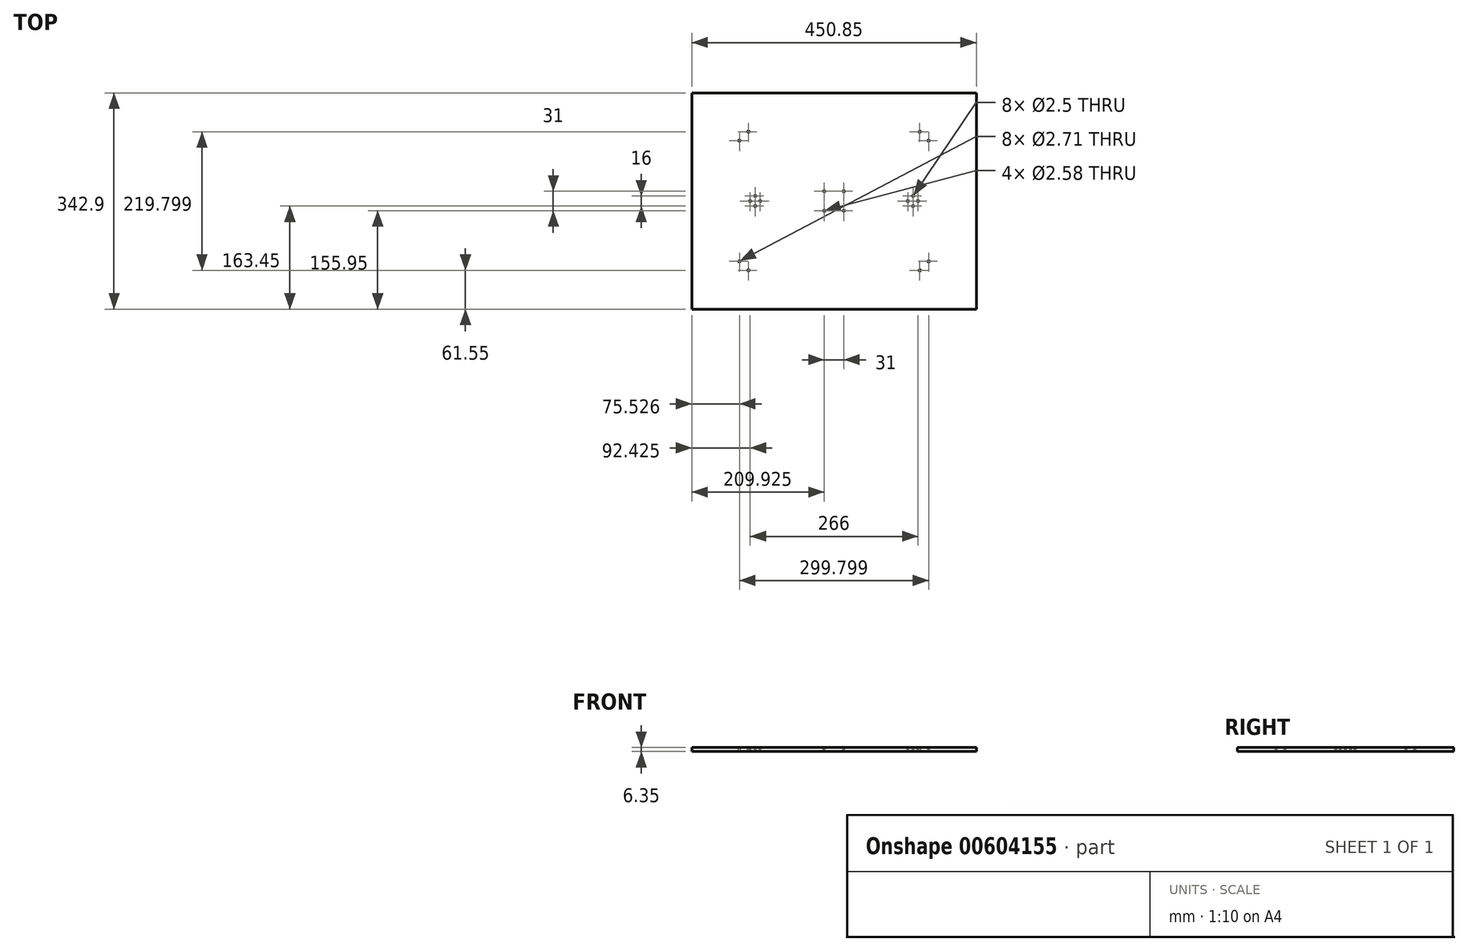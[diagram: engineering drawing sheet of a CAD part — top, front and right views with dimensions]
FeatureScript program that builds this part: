
annotation { "Feature Type Name" : "Feature", "Feature Type Description" : "" }
export const myFeature = defineFeature(function(context is Context, id is Id, definition is map)
    precondition{}
    {
        {
            var Q0;
            Q0=qCreatedBy(makeId("Top.planeOp"),FACE);
            var sketch = newSketch(context, id + "F0", { "sketchPlane" : qUnion([Q0])});
            skLineSegment(sketch, "E0.bottom", {"start": v(0, 0) * mm, "end": v(-450.85, 0) * mm});
            skLineSegment(sketch, "E0.top", {"start": v(0, -342.9) * mm, "end": v(-450.85, -342.9) * mm});
            skLineSegment(sketch, "E0.left", {"start": v(0, 0) * mm, "end": v(0, -342.9) * mm});
            skLineSegment(sketch, "E0.right", {"start": v(-450.85, 0) * mm, "end": v(-450.85, -342.9) * mm});
            skSolve(sketch);
        }
        {
            var Q0;
            Q0 = qSketchRegion(id + "F0", true);
            extrude(context, id + "F1", {"entities" : qUnion([Q0]), "depth" : 6.35 * mm, "offsetDistance" : 25 * mm});
        }
        {
            var Q0;
            Q0=makeQuery(id+"F1.opExtrude","CAP_FACE",FACE,{"disambiguationData":[OSD([sQuery(id+"F0.wireOp",EDGE,"E0.bottom"),sQuery(id+"F0.wireOp",EDGE,"E0.top"),sQuery(id+"F0.wireOp",EDGE,"E0.left"),sQuery(id+"F0.wireOp",EDGE,"E0.right")])],"isStart":false});
            var sketch = newSketch(context, id + "F2", { "sketchPlane" : qUnion([Q0])});
            skLineSegment(sketch, "E1", {"start": v(-225.43, 0) * mm, "end": v(-225.42, -342.9) * mm, "construction": true});
            skLineSegment(sketch, "E2", {"start": v(-450.85, -171.45) * mm, "end": v(0, -171.45) * mm, "construction": true});
            skPoint(sketch, "E3", {"position": v(-225.42, -171.45) * mm});
            skLineSegment(sketch, "E4.bottom", {"start": v(-225.42, -171.45) * mm, "end": v(-240.92, -171.45) * mm, "construction": true});
            skLineSegment(sketch, "E4.top", {"start": v(-225.42, -155.95) * mm, "end": v(-240.93, -155.95) * mm, "construction": true});
            skLineSegment(sketch, "E4.left", {"start": v(-225.42, -171.45) * mm, "end": v(-225.42, -155.95) * mm, "construction": true});
            skLineSegment(sketch, "E4.right", {"start": v(-240.92, -171.45) * mm, "end": v(-240.92, -155.95) * mm, "construction": true});
            skLineSegment(sketch, "E5.MirrorCS", {"start": v(-225.42, -155.95) * mm, "end": v(-209.92, -155.95) * mm, "construction": true});
            skLineSegment(sketch, "E6.MirrorCS", {"start": v(-209.93, -171.45) * mm, "end": v(-209.93, -155.95) * mm, "construction": true});
            skLineSegment(sketch, "E7.MirrorCS", {"start": v(-225.42, -186.95) * mm, "end": v(-209.92, -186.95) * mm, "construction": true});
            skLineSegment(sketch, "E8.MirrorCS", {"start": v(-225.42, -186.95) * mm, "end": v(-240.93, -186.95) * mm, "construction": true});
            skLineSegment(sketch, "E9.MirrorCS", {"start": v(-240.92, -171.45) * mm, "end": v(-240.92, -186.95) * mm, "construction": true});
            skLineSegment(sketch, "E10.MirrorCS", {"start": v(-209.93, -171.45) * mm, "end": v(-209.93, -186.95) * mm, "construction": true});
            skLineSegment(sketch, "E11", {"start": v(-225.42, -171.45) * mm, "end": v(-350.42, -171.45) * mm, "construction": true});
            skLineSegment(sketch, "E12", {"start": v(-225.42, -171.45) * mm, "end": v(-100.42, -171.45) * mm, "construction": true});
            skCircle(sketch, "E13", {"center": v(-350.42, -171.45) * mm, "radius": 8 * mm, "construction": true});
            skCircle(sketch, "E14", {"center": v(-100.42, -171.45) * mm, "radius": 8 * mm, "construction": true});
            skPoint(sketch, "E15", {"position": v(-342.42, -171.45) * mm});
            skPoint(sketch, "E16", {"position": v(-358.42, -171.45) * mm});
            skLineSegment(sketch, "E17", {"start": v(-350.42, -163.45) * mm, "end": v(-350.42, -179.45) * mm, "construction": true});
            skPoint(sketch, "E18", {"position": v(-350.42, -163.45) * mm});
            skPoint(sketch, "E19", {"position": v(-350.42, -179.45) * mm});
            skPoint(sketch, "E20.MirrorP", {"position": v(-100.42, -163.45) * mm});
            skPoint(sketch, "E21.MirrorP", {"position": v(-92.42, -171.45) * mm});
            skPoint(sketch, "E22.MirrorP", {"position": v(-100.42, -179.45) * mm});
            skPoint(sketch, "E23.MirrorP", {"position": v(-108.42, -171.45) * mm});
            skLineSegment(sketch, "E24", {"start": v(-225.42, -171.45) * mm, "end": v(-225.42, -281.35) * mm, "construction": true});
            skLineSegment(sketch, "E25", {"start": v(-225.42, -171.45) * mm, "end": v(-225.42, -61.45) * mm, "construction": true});
            skLineSegment(sketch, "E26", {"start": v(-225.42, -171.45) * mm, "end": v(-225.42, -267.2) * mm, "construction": true});
            skLineSegment(sketch, "E27", {"start": v(-225.42, -171.45) * mm, "end": v(-225.42, -75.59) * mm, "construction": true});
            skLineSegment(sketch, "E28", {"start": v(-225.42, -267.2) * mm, "end": v(-375.32, -267.2) * mm, "construction": true});
            skLineSegment(sketch, "E29", {"start": v(-225.42, -281.35) * mm, "end": v(-361.18, -281.35) * mm, "construction": true});
            skLineSegment(sketch, "E30", {"start": v(-225.42, -171.45) * mm, "end": v(-402.25, -171.45) * mm, "construction": true});
            skLineSegment(sketch, "E31.MirrorCS", {"start": v(-225.42, -75.7) * mm, "end": v(-375.32, -75.7) * mm, "construction": true});
            skLineSegment(sketch, "E32.MirrorCS", {"start": v(-225.42, -61.55) * mm, "end": v(-361.18, -61.55) * mm, "construction": true});
            skLineSegment(sketch, "E33.MirrorCS", {"start": v(-225.42, -61.55) * mm, "end": v(-89.67, -61.55) * mm, "construction": true});
            skLineSegment(sketch, "E34.MirrorCS", {"start": v(-225.42, -75.7) * mm, "end": v(-75.53, -75.7) * mm, "construction": true});
            skLineSegment(sketch, "E35.MirrorCS", {"start": v(-225.42, -267.2) * mm, "end": v(-75.53, -267.2) * mm, "construction": true});
            skLineSegment(sketch, "E36.MirrorCS", {"start": v(-225.42, -281.35) * mm, "end": v(-89.67, -281.35) * mm, "construction": true});
            skSolve(sketch);
        }
        {
            var Q0;
            Q0=sQuery(id+"F2.wireOp",VERTEX,"E4.right.end");
            var Q1;
            Q1=sQuery(id+"F2.wireOp",VERTEX,"E6.MirrorCS.end");
            var Q2;
            Q2=sQuery(id+"F2.wireOp",VERTEX,"E7.MirrorCS.end");
            var Q3;
            Q3=sQuery(id+"F2.wireOp",VERTEX,"E8.MirrorCS.end");
            var Q4;
            Q4=makeQuery(id+"F1.opExtrude","SWEPT_BODY",BODY,{"disambiguationData":[OSD([sQuery(id+"F0.wireOp",EDGE,"E0.bottom"),sQuery(id+"F0.wireOp",EDGE,"E0.top"),sQuery(id+"F0.wireOp",EDGE,"E0.left"),sQuery(id+"F0.wireOp",EDGE,"E0.right")])]});
            hole(context, id + "F3", {"style" : HoleStyle.SIMPLE, "endStyle" : HoleEndStyle.BLIND, "standardTappedOrClearance" : lookupTablePath({ "standard" : "ANSI", "engagement" : "75%", "pitch" : "40 tpi", "size" : "#5", "type" : "Tapped" }), "standardBlindInLast" : lookupTablePath({ "standard" : "ANSI", "engagement" : "75%", "pitch" : "40 tpi", "size" : "#5", "type" : "Tapped" }), "holeDiameter" : 2.58 * mm, "majorDiameter" : 3.17 * mm, "showTappedDepth" : true, "holeDepth" : 13.9 * mm, "tappedDepth" : 12 * mm, "tapClearance" : 3, "locations" : qUnion([Q0, Q1, Q2, Q3]), "scope" : qUnion([Q4])});
        }
        {
            var Q0;
            Q0=sQuery(id+"F2.wireOp",VERTEX,"E15");
            var Q1;
            Q1=sQuery(id+"F2.wireOp",VERTEX,"E16");
            var Q2;
            Q2=sQuery(id+"F2.wireOp",VERTEX,"E18");
            var Q3;
            Q3=sQuery(id+"F2.wireOp",VERTEX,"E19");
            var Q4;
            Q4=makeQuery(id+"F1.opExtrude","SWEPT_BODY",BODY,{"disambiguationData":[OSD([sQuery(id+"F0.wireOp",EDGE,"E0.bottom"),sQuery(id+"F0.wireOp",EDGE,"E0.top"),sQuery(id+"F0.wireOp",EDGE,"E0.left"),sQuery(id+"F0.wireOp",EDGE,"E0.right")])]});
            hole(context, id + "F4", {"style" : HoleStyle.SIMPLE, "endStyle" : HoleEndStyle.THROUGH, "standardTappedOrClearance" : lookupTablePath({ "standard" : "ISO", "engagement" : "75%", "pitch" : "0.5 mm", "size" : "M3", "type" : "Tapped" }), "standardBlindInLast" : lookupTablePath({ "standard" : "ISO", "engagement" : "75%", "pitch" : "0.5 mm", "size" : "M3", "type" : "Tapped" }), "holeDiameter" : 2.5 * mm, "majorDiameter" : 3 * mm, "showTappedDepth" : true, "isTappedThrough" : true, "tappedDepth" : 12 * mm, "tapClearance" : 3, "locations" : qUnion([Q0, Q1, Q2, Q3]), "scope" : qUnion([Q4])});
        }
        {
            var Q0;
            Q0=sQuery(id+"F2.wireOp",VERTEX,"E20.MirrorP");
            var Q1;
            Q1=sQuery(id+"F2.wireOp",VERTEX,"E23.MirrorP");
            var Q2;
            Q2=sQuery(id+"F2.wireOp",VERTEX,"E22.MirrorP");
            var Q3;
            Q3=sQuery(id+"F2.wireOp",VERTEX,"E21.MirrorP");
            var Q4;
            Q4=makeQuery(id+"F1.opExtrude","SWEPT_BODY",BODY,{"disambiguationData":[OSD([sQuery(id+"F0.wireOp",EDGE,"E0.bottom"),sQuery(id+"F0.wireOp",EDGE,"E0.top"),sQuery(id+"F0.wireOp",EDGE,"E0.left"),sQuery(id+"F0.wireOp",EDGE,"E0.right")])]});
            hole(context, id + "F5", {"style" : HoleStyle.SIMPLE, "endStyle" : HoleEndStyle.THROUGH, "standardTappedOrClearance" : lookupTablePath({ "standard" : "ISO", "engagement" : "75%", "pitch" : "0.5 mm", "size" : "M3", "type" : "Tapped" }), "standardBlindInLast" : lookupTablePath({ "standard" : "ISO", "engagement" : "75%", "pitch" : "0.5 mm", "size" : "M3", "type" : "Tapped" }), "holeDiameter" : 2.5 * mm, "majorDiameter" : 3 * mm, "showTappedDepth" : true, "isTappedThrough" : true, "tappedDepth" : 12 * mm, "tapClearance" : 3, "locations" : qUnion([Q0, Q1, Q2, Q3]), "scope" : qUnion([Q4])});
        }
        {
            var Q0;
            Q0=sQuery(id+"F2.wireOp",VERTEX,"E32.MirrorCS.end");
            var Q1;
            Q1=sQuery(id+"F2.wireOp",VERTEX,"E31.MirrorCS.end");
            var Q2;
            Q2=sQuery(id+"F2.wireOp",VERTEX,"E33.MirrorCS.end");
            var Q3;
            Q3=sQuery(id+"F2.wireOp",VERTEX,"E34.MirrorCS.end");
            var Q4;
            Q4=sQuery(id+"F2.wireOp",VERTEX,"E35.MirrorCS.end");
            var Q5;
            Q5=sQuery(id+"F2.wireOp",VERTEX,"E36.MirrorCS.end");
            var Q6;
            Q6=sQuery(id+"F2.wireOp",VERTEX,"E29.end");
            var Q7;
            Q7=sQuery(id+"F2.wireOp",VERTEX,"E28.end");
            var Q8;
            Q8=makeQuery(id+"F1.opExtrude","SWEPT_BODY",BODY,{"disambiguationData":[OSD([sQuery(id+"F0.wireOp",EDGE,"E0.bottom"),sQuery(id+"F0.wireOp",EDGE,"E0.top"),sQuery(id+"F0.wireOp",EDGE,"E0.left"),sQuery(id+"F0.wireOp",EDGE,"E0.right")])]});
            hole(context, id + "F6", {"style" : HoleStyle.SIMPLE, "endStyle" : HoleEndStyle.THROUGH, "standardTappedOrClearance" : lookupTablePath({ "standard" : "ANSI", "engagement" : "75%", "pitch" : "32 tpi", "size" : "#6", "type" : "Tapped" }), "standardBlindInLast" : lookupTablePath({ "standard" : "ANSI", "engagement" : "75%", "pitch" : "32 tpi", "size" : "#6", "type" : "Tapped" }), "holeDiameter" : 2.7 * mm, "majorDiameter" : 3.5 * mm, "showTappedDepth" : true, "isTappedThrough" : true, "tappedDepth" : 12 * mm, "tapClearance" : 3, "locations" : qUnion([Q0, Q1, Q2, Q3, Q4, Q5, Q6, Q7]), "scope" : qUnion([Q8])});
        }
    });
